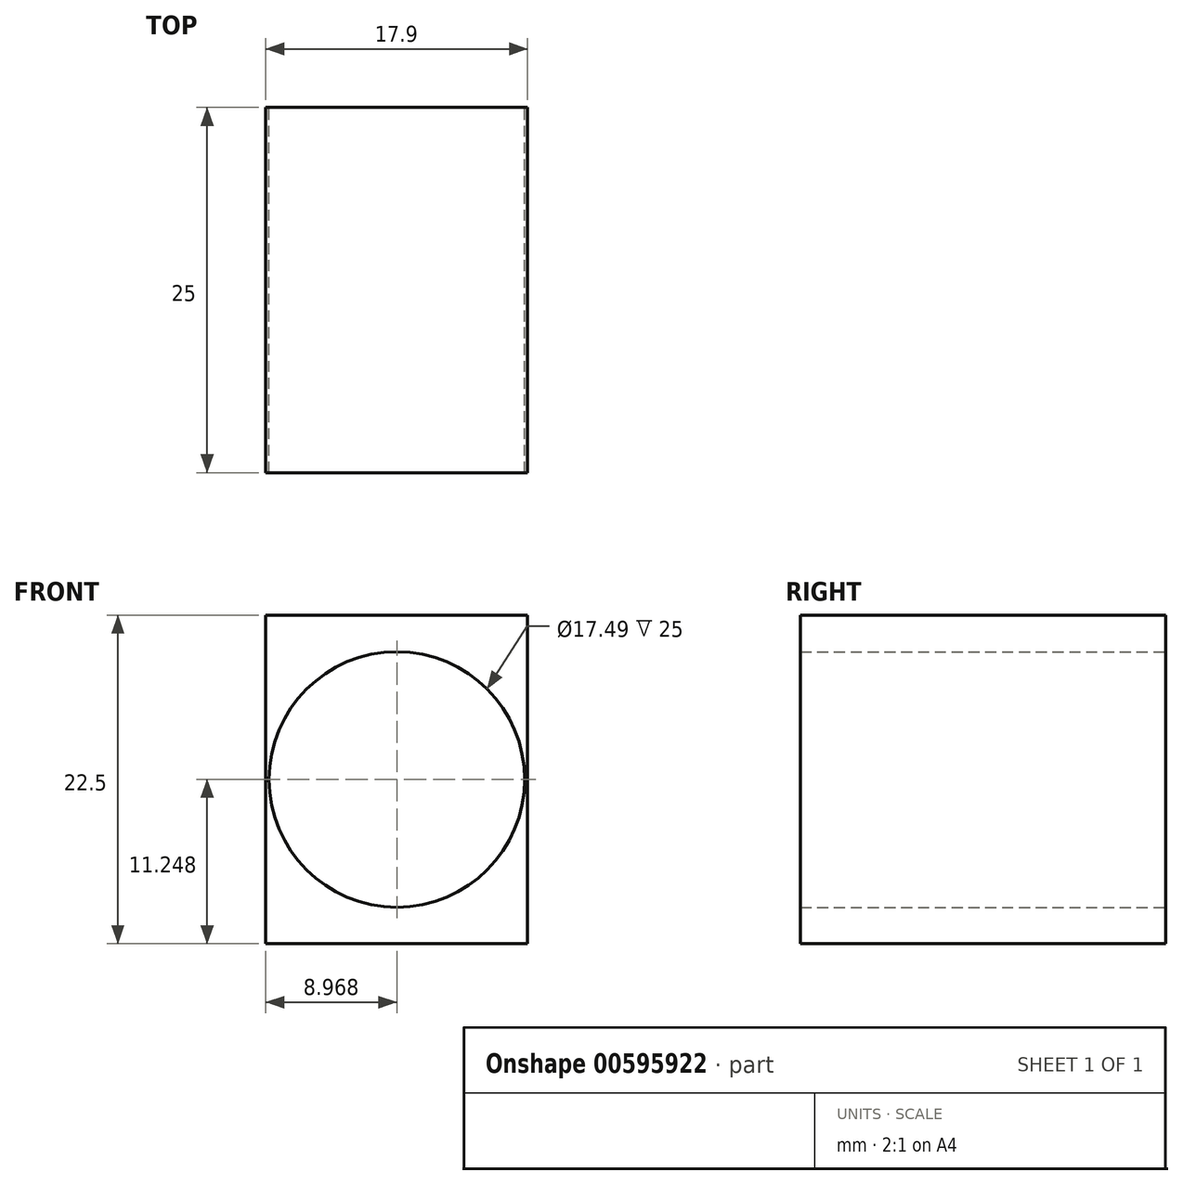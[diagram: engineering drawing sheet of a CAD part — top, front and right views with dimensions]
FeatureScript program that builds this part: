
annotation { "Feature Type Name" : "Feature", "Feature Type Description" : "" }
export const myFeature = defineFeature(function(context is Context, id is Id, definition is map)
    precondition{}
    {
        {
            var Q0;
            Q0=qCreatedBy(makeId("Front.planeOp"),FACE);
            var sketch = newSketch(context, id + "F0", { "sketchPlane" : qUnion([Q0])});
            skLineSegment(sketch, "E0.bottom", {"start": v(0, 0) * mm, "end": v(-17.9, 0) * mm});
            skLineSegment(sketch, "E0.top", {"start": v(0, 22.5) * mm, "end": v(-17.9, 22.5) * mm});
            skLineSegment(sketch, "E0.left", {"start": v(0, 0) * mm, "end": v(0, 22.5) * mm});
            skLineSegment(sketch, "E0.right", {"start": v(-17.9, 0) * mm, "end": v(-17.9, 22.5) * mm});
            skCircle(sketch, "E1", {"center": v(-8.93, 11.25) * mm, "radius": 8.74 * mm});
            skSolve(sketch);
        }
        {
            var Q0;
            Q0=qSketchRegion(id+"F0",true);
            extrude(context, id + "F1", {"entities" : qUnion([Q0]), "depth" : 25 * mm, "offsetDistance" : 25 * mm});
        }
    });
